# Revit family: JC KONTAKTER JCK257 Armbågskontakt
name_source: partatom
category: Specialty Equipment
units: mm (PartAtom-declared; Revit-internal decimal feet)

## family parameters
Always vertical = Yes
Cut with Voids When Loaded = No
Enable Cutting in Views = Yes
Host = Wall
Maintain Annotation Orientation = No
Part Type = Normal
Room Calculation Point = No
Round Connector Dimension = Use Diameter
Shared = No

## types (2) — shared parameters
Antal mikrobrytare = 2
CE Dokument = https://jckontakter.se
Core Finish = Aluminum ENAW 6060
Lägsta märkström = 1mA/4 V DC
Manufacturer = JC Kontakter
Mikrobrytare = Standard NO IP67
Placering av armbågskontakt = https://jckontakter.se
Tekniskt produktblad = https://jckontakter.se
Tillvalsförteckning = https://jckontakter.se
Tillverkningsland = Sverige
URL = https://jckontakter.se
zero-valued in all types: Default Elevation

## per-type parameters (varying)
| type | Description | End Cap Finish | Lid Finish | Model | Nominell märkström | Produktvikt |
| Armbågskontakt JCK247 | JCK247 har två tryckytor och är tillverkad i silvereloxerad aluminium med svarta endcaps. Båda tryckytorna är utformade med fyra taktila rillor och fungerar som extra vägledning för personer med synnedsättning. Man kan enkelt känna sig till vart man ska trycka för att aktivera dörröppning.

JCK247 ingår i en produktserie av armbågskontakter med två tryckytor som är lika stora. Serien är särskilt utvecklad för miljöer med dubbla slagdörrar och gör det möjligt att styra varje dörr separat med en egen tryckknapp. Funktionen bidrar till att minska kallras och drag, samt spar energi jämfört med att båda dörrar åker upp vid varje öppning. Dessa armbågskontakter kan även vara lämpliga i en passage där det finns två ingångar till lokalen. | POM Tenac C 4520 | Aluminum ENAW 6060 | JCK247 | 0,1A - 10 A/250 V AC | 0.766 kg. |
| Armbågskontakt JCK257 | JCK257 har två tryckytor och är tillverkad i silvereloxerad aluminium med svarta endcaps. Båda tryckytorna är utformade med fyra taktila rillor och fungerar som extra vägledning för personer med synnedsättning. Man kan enkelt känna sig till vart man ska trycka för att aktivera dörröppning.

JCK247 ingår i en produktserie av armbågskontakter med två tryckytor som är lika stora. Serien är särskilt utvecklad för miljöer med dubbla slagdörrar och gör det möjligt att styra varje dörr separat med en egen tryckknapp. Funktionen bidrar till att minska kallras och drag, samt spar energi jämfört med att båda dörrar åker upp vid varje öppning. Dessa armbågskontakter kan även vara lämpliga i en passage där det finns två ingångar till lokalen. | POM Tenac C 4520 (Vit) | Aluminum ENAW 6060 (Svart) | JCK257 | 12 V - Resistive 6A Inductive L/R 5ms 6A, 24 V - Resistive 6A Inductive L/R 5ms 5A | 0.766 kg |

## geometry (parser evidence)
native form markers: Sweep x4
no freeform markers — native parametric forms only
